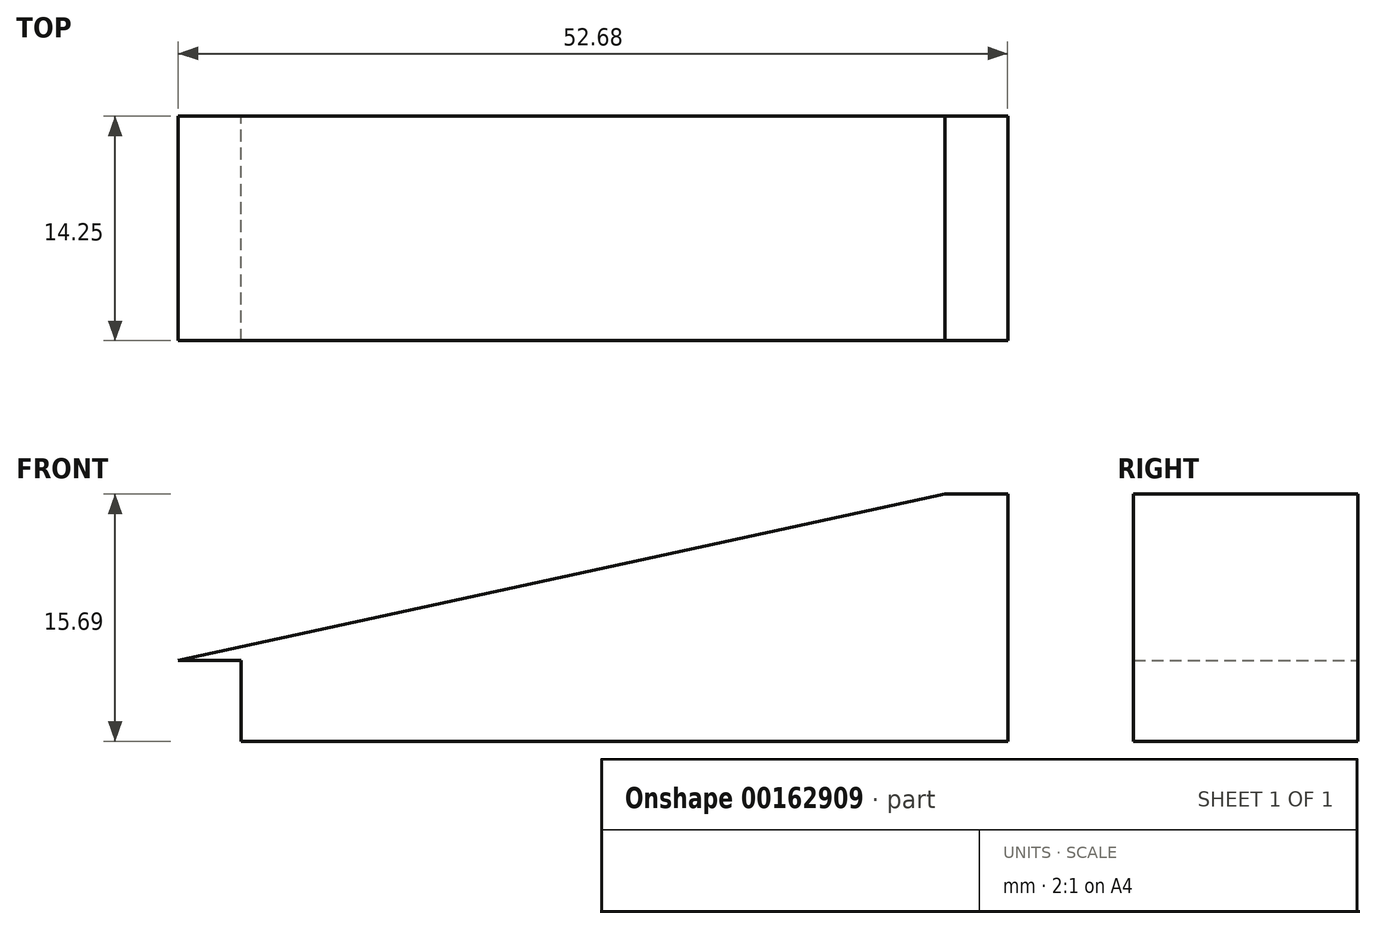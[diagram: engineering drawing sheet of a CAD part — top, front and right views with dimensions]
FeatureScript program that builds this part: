
annotation { "Feature Type Name" : "Feature", "Feature Type Description" : "" }
export const myFeature = defineFeature(function(context is Context, id is Id, definition is map)
    precondition{}
    {
        {
            var Q0;
            Q0=qCreatedBy(makeId("Front.planeOp"),FACE);
            var sketch = newSketch(context, id + "F0", { "sketchPlane" : qUnion([Q0])});
            skLineSegment(sketch, "E0", {"start": v(22.58, 0) * mm, "end": v(-26.1, 0) * mm});
            skLineSegment(sketch, "E1", {"start": v(-26.1, 0) * mm, "end": v(-26.1, 5.13) * mm});
            skLineSegment(sketch, "E2", {"start": v(-26.1, 5.13) * mm, "end": v(22.58, 15.7) * mm});
            skLineSegment(sketch, "E3", {"start": v(22.58, 15.7) * mm, "end": v(22.58, 0) * mm});
            skSolve(sketch);
        }
        {
            var Q0;
            Q0=makeQuery(id+"F0.imprint","IMPRINT",FACE,{"disambiguationData":[TD([[makeQuery(id+"F0.imprint","IMPRINT",EDGE,{"derivedFrom":sQuery(id+"F0.wireOp",EDGE,"E0")}),-1.0]])]});
            extrude(context, id + "F1", {"entities" : qUnion([Q0]), "depth" : 14.25 * mm});
        }
        {
            var Q0;
            Q0=makeQuery(id+"F1.opExtrude","SWEPT_FACE",FACE,{"disambiguationData":[OSD([sQuery(id+"F0.wireOp",EDGE,"E3")])]});
            var sketch = newSketch(context, id + "F2", { "sketchPlane" : qUnion([Q0])});
            skSolve(sketch);
        }
        {
            var Q0;
            {var subQ0=sQuery(id+"F0.wireOp",EDGE,"E3");Q0=makeQuery(id+"F2.imprint","IMPRINT",FACE,{"disambiguationData":[TD([[makeQuery(id+"F2.imprint","IMPRINT",EDGE,{"derivedFrom":makeQuery(id+"F1.opExtrude","CAP_EDGE",EDGE,{"disambiguationData":[OSD([subQ0])],"isStart":true})}),-1.0]])]});}
            var sketch = newSketch(context, id + "F3", { "sketchPlane" : qUnion([Q0])});
            skCircle(sketch, "E4", {"center": v(-7.36, 8.11) * mm, "radius": 2.63 * mm});
            skSolve(sketch);
        }
        {
            var Q0;
            Q0 = qSketchRegion(id + "F3", true);
            var Q1;
            {var subQ0=sQuery(id+"F0.wireOp",EDGE,"E3");Q1=makeQuery(id+"F2.imprint","IMPRINT",FACE,{"disambiguationData":[TD([[makeQuery(id+"F2.imprint","IMPRINT",EDGE,{"derivedFrom":makeQuery(id+"F1.opExtrude","CAP_EDGE",EDGE,{"disambiguationData":[OSD([subQ0])],"isStart":true})}),-1.0]])]});}
            var Q2;
            Q2=makeQuery(id+"F1.opExtrude","SWEPT_FACE",FACE,{"disambiguationData":[OSD([sQuery(id+"F0.wireOp",EDGE,"E2")])]});
            extrude(context, id + "F4", {"entities" : qUnion([Q0, Q1, Q2]), "operationType" : NewBodyOperationType.ADD, "oppositeDirection" : true, "depth" : 4 * mm});
        }
    });
